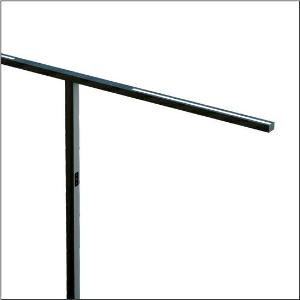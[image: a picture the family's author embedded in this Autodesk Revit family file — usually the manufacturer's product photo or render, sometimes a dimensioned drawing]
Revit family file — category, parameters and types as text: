
# Revit family: silica_r__31_floor_duo_51my52hmtcb_73f4
name_source: partatom
category: Lighting Fixtures
units: mm (PartAtom-declared; Revit-internal decimal feet)

## family parameters
Cut with Voids When Loaded = No
Host = Face
Light Source = No
Part Type = Normal
Room Calculation Point = No
Round Connector Dimension = Use Diameter
Shared = No

## types (1)
- --- (1 x LED, 17040 lm, 142 W, 4000K)
    Apparent Load = 142 VA
    CIE Flux Codes = 86 100 100 24 100
    Color Rendering = 80
    Color Temperature = 4000K
    Default Elevation = 1800 mm
    Description = Silica® 31 Floor duo, floorstanding luminaire, secondary optical cover: cover panel, of PMMA, light emission: direct/indirect distribution, primary light characteristic: symmetric, installation type: not mounted, LED, rated luminous flux: 17.040lm, luminous efficacy: 120lm/W, light colour: 8tw, colour temperature: 2700..6500K, daylight-dependent control, with cable with plug, mains connection: 230V, AC, 50Hz, rated input power: 142W, luminaire head, of aluminium, coated, jet black (RAL 9005), length: 1.203mm, width: 52mm, supporting column, angular, of aluminium, coated, jet black (RAL 9005), baseplate, of steel, coated, jet black (RAL 9005), protection rating (complete): IP20, insulation class (complete): insulation class I (protective earthing), certification: CE, permissible operating ambient temperature: -20..+40°C, standard: EN 50419, packaging unit: 1 piece
    Height = 36 mm
    Lamp = 1 x LED
    Lamp Light Flux = 17040 lm
    Lamp Power = 142 W
    Lamp count = 1
    Length = 2372 mm
    Luminous efficacy = 120 lm/W
    Manufacturer = Siteco
    ModVariant = No
    Model = 51MY52HMTCB
    Mounting Place = Floor
    Mounting Type = Freestanding
    Number of Poles = 1
    OnlyDefault = Yes
    Power Factor = 1
    Product Name = Silica® 31 Floor duo
    Product group = floorstanding luminaire
    ProductGroupID = 1301
    Protection Class = Protection class I
    Protection Degree = IP 20
    RLX_Detail_Level = 1
    RLX_Emergency_Light_Flux = 0 lm
    RLX_Emergency_Type = 0
    RLX_Emergency_Type_DB = No
    RlxData = <blob elided: 21585 chars, md5=8d48bc07>
    Socket = socket
    Standby Power = 0 W
    System Light Flux = 17040 lm
    System Power = 142 W
    Type Comments = factory setting
    Type Image = l_1275315.jpg
    URL = http://relux.com
    VarID = @adj_013765
    Voltage = 0 V
    Weight = 0.00 kg
    Width = 52 mm  [stored 0.170604 ft]

note: [stored X ft] marks values corroborated as IEEE doubles in the binary element streams (Revit-internal decimal feet)

## geometry (parser evidence)
native form markers: Blend x4, Sweep x13
no freeform markers — native parametric forms only
